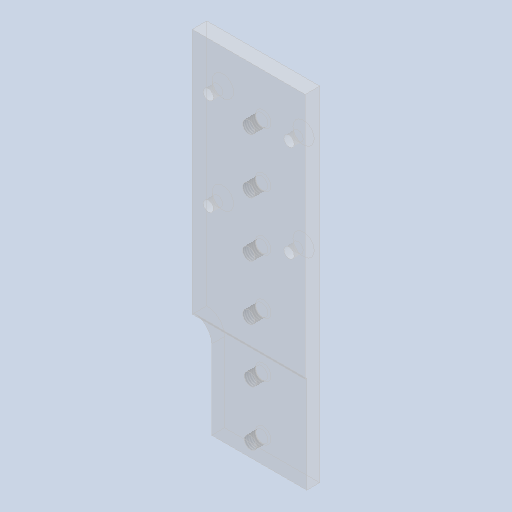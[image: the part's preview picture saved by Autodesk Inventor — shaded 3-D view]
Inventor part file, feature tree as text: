
AUTODESK INVENTOR PART (.ipt)
format: ipt  version: 2022 (Build 260153000, 153)  size: 148,480 bytes
history: native  units: in
note: dims shown in document units (in); Inventor stores cm internally (conversion verified against a paired STEP export)
features: other x4, sketch x2, plane x1
ambient origin geometry x8: Origin, YZ Plane, XZ Plane, XY Plane, X Axis, Y Axis, Z Axis, Center Point
bodies: Solid1 (feature_tree)
feature tree (7):
  other  "Plate.ipt"
  other  "Solid1::Plate.ipt"
  other  "TaggingFeature1"
  sketch  "Sketch1"  dims[d0=0.3937in]
  sketch  "Sketch2"
  plane  "Work Plane1"
  other  "Work Axis1"
